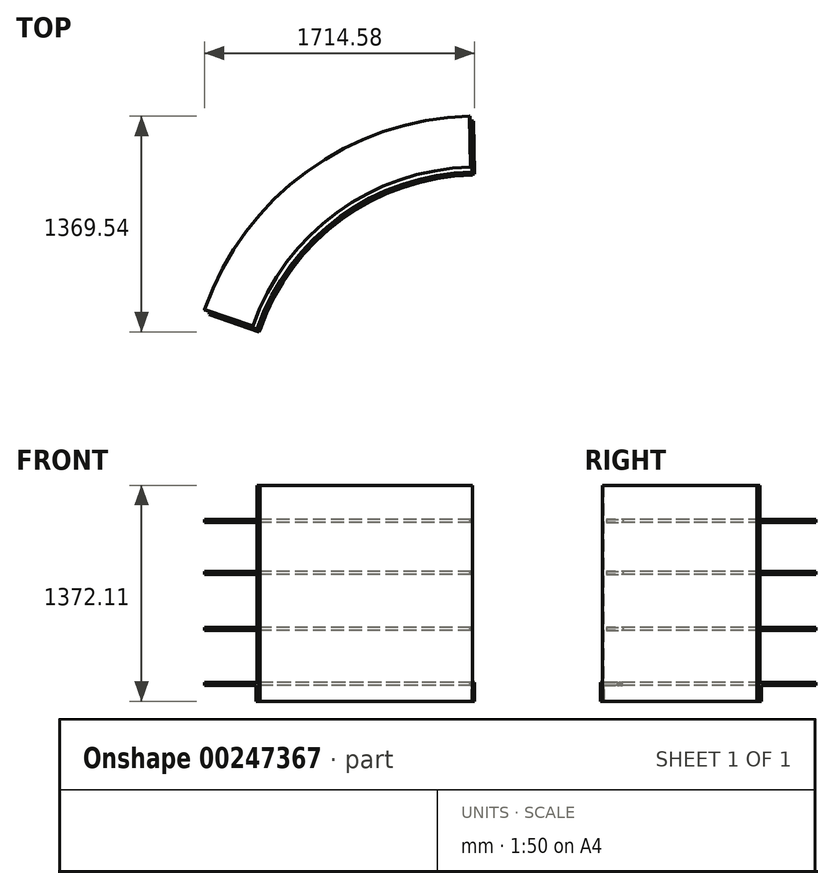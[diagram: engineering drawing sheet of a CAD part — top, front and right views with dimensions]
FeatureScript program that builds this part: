
annotation { "Feature Type Name" : "Feature", "Feature Type Description" : "" }
export const myFeature = defineFeature(function(context is Context, id is Id, definition is map)
    precondition{}
    {
        {
            var Q0;
            Q0=qCreatedBy(makeId("Top.planeOp"),FACE);
            var sketch = newSketch(context, id + "F0", { "sketchPlane" : qUnion([Q0])});
            skCircle(sketch, "E0", {"center": v(0, 0) * mm, "radius": 1828.8 * mm});
            skLineSegment(sketch, "E1", {"start": v(0, 0) * mm, "end": v(-35, 1828.47) * mm});
            skLineSegment(sketch, "E2", {"start": v(0, 0) * mm, "end": v(-1730.17, 592.48) * mm});
            skCircle(sketch, "E3", {"center": v(0, 0) * mm, "radius": 1473.2 * mm});
            skCircle(sketch, "E4", {"center": v(0, 0) * mm, "radius": 1492.76 * mm});
            skLineSegment(sketch, "E5.0", {"start": v(2.06, 6) * mm, "end": v(-1728.1, 598.5) * mm});
            skLineSegment(sketch, "E6.0", {"start": v(-6.35, -0.12) * mm, "end": v(-41.35, 1828.34) * mm});
            skLineSegment(sketch, "E7", {"start": v(-40.62, 1790.24) * mm, "end": v(-34.27, 1790.37) * mm});
            skLineSegment(sketch, "E8", {"start": v(-1692.06, 586.15) * mm, "end": v(-1694.12, 580.14) * mm});
            skCircle(sketch, "E9", {"center": v(-85.5, 1480.26) * mm, "radius": 2.5 * mm});
            skCircle(sketch, "E10.1.0", {"center": v(-270.91, 1457.77) * mm, "radius": 2.5 * mm});
            skCircle(sketch, "E10.2.0", {"center": v(-452.03, 1412.14) * mm, "radius": 2.5 * mm});
            skCircle(sketch, "E10.3.0", {"center": v(-625.97, 1344.1) * mm, "radius": 2.5 * mm});
            skCircle(sketch, "E10.4.0", {"center": v(-789.99, 1254.75) * mm, "radius": 2.5 * mm});
            skCircle(sketch, "E10.5.0", {"center": v(-941.46, 1145.48) * mm, "radius": 2.5 * mm});
            skCircle(sketch, "E10.6.0", {"center": v(-1078, 1018.03) * mm, "radius": 2.5 * mm});
            skCircle(sketch, "E10.7.0", {"center": v(-1197.43, 874.43) * mm, "radius": 2.5 * mm});
            skCircle(sketch, "E10.8.0", {"center": v(-1297.86, 716.95) * mm, "radius": 2.5 * mm});
            skCircle(sketch, "E10.9.0", {"center": v(-1377.7, 548.1) * mm, "radius": 2.5 * mm});
            skLineSegment(sketch, "E10.anchor1", {"start": v(0, 0) * mm, "end": v(-85.5, 1480.26) * mm, "construction": true});
            skLineSegment(sketch, "E10.anchor2", {"start": v(0, 0) * mm, "end": v(-1377.7, 548.1) * mm, "construction": true});
            skLineSegment(sketch, "E11.0", {"start": v(3.09, 9.01) * mm, "end": v(-1727.08, 601.5) * mm});
            skLineSegment(sketch, "E12.0", {"start": v(-9.52, -0.18) * mm, "end": v(-44.52, 1828.28) * mm});
            skCircle(sketch, "E13.0", {"center": v(0, 0) * mm, "radius": 1505.46 * mm});
            skCircle(sketch, "E14.0", {"center": v(0, 0) * mm, "radius": 1453.64 * mm});
            skLineSegment(sketch, "E15", {"start": v(2.06, 6) * mm, "end": v(-758.66, 1049.34) * mm});
            skSolve(sketch);
        }
        {
            var Q0;
            {var subQ0=sQuery(id+"F0.wireOp",EDGE,"E12.0");var subQ1=sQuery(id+"F0.wireOp",EDGE,"E0");var subQ2=makeQuery(id+"F0.imprint","INTERSECT",VERTEX,{"derivedFrom":[subQ1,subQ0]});Q0=makeQuery(id+"F0.imprint","IMPRINT",FACE,{"disambiguationData":[TD([[makeQuery(id+"F0.imprint","IMPRINT",EDGE,{"disambiguationData":[TD([[subQ2,-1.0]])],"derivedFrom":subQ1}),1.0]])]});}
            extrude(context, id + "F1", {"entities" : qUnion([Q0]), "depth" : 19.56 * mm});
        }
        {
            var Q0;
            Q0=makeQuery(id+"F1.opExtrude","SWEPT_BODY",BODY,{"disambiguationData":[OSD([sQuery(id+"F0.wireOp",EDGE,"E0"),sQuery(id+"F0.wireOp",EDGE,"E4"),sQuery(id+"F0.wireOp",EDGE,"E11.0"),sQuery(id+"F0.wireOp",EDGE,"E12.0")])]});
            transform(context, id + "F2", {"entities" : qUnion([Q0]), "transformType" : TransformType.TRANSLATION_3D, "dx" : 0 * mm, "dy" : 0 * mm, "dz" : 508 * mm, "makeCopy" : false});
        }
        {
            var Q0;
            {var subQ0=sQuery(id+"F0.wireOp",EDGE,"E12.0");var subQ1=sQuery(id+"F0.wireOp",EDGE,"E0");var subQ2=makeQuery(id+"F0.imprint","INTERSECT",VERTEX,{"derivedFrom":[subQ1,subQ0]});Q0=makeQuery(id+"F0.imprint","IMPRINT",FACE,{"disambiguationData":[TD([[makeQuery(id+"F0.imprint","IMPRINT",EDGE,{"disambiguationData":[TD([[subQ2,-1.0]])],"derivedFrom":subQ1}),1.0]])]});}
            var Q1;
            {var subQ2=sQuery(id+"F0.wireOp",EDGE,"E0");var subQ6=sQuery(id+"F0.wireOp",EDGE,"E11.0");var subQ8=makeQuery(id+"F0.imprint","INTERSECT",VERTEX,{"derivedFrom":[subQ2,subQ6]});Q1=makeQuery(id+"F0.imprint","IMPRINT",FACE,{"disambiguationData":[TD([[makeQuery(id+"F0.imprint","IMPRINT",EDGE,{"disambiguationData":[TD([[subQ8,-1.0]])],"derivedFrom":subQ2}),1.0]])]});}
            var Q2;
            {var subQ0=sQuery(id+"F0.wireOp",EDGE,"E8");Q2=makeQuery(id+"F0.imprint","IMPRINT",FACE,{"disambiguationData":[TD([[makeQuery(id+"F0.imprint","IMPRINT",EDGE,{"derivedFrom":subQ0}),1.0]])]});}
            var Q3;
            {var subQ0=sQuery(id+"F0.wireOp",EDGE,"E3");var subQ1=sQuery(id+"F0.wireOp",EDGE,"E2");var subQ2=makeQuery(id+"F0.imprint","INTERSECT",VERTEX,{"derivedFrom":[subQ1,subQ0]});Q3=makeQuery(id+"F0.imprint","IMPRINT",FACE,{"disambiguationData":[TD([[makeQuery(id+"F0.imprint","IMPRINT",EDGE,{"disambiguationData":[TD([[subQ2,-1.0]])],"derivedFrom":subQ1}),-1.0]])]});}
            var Q4;
            {var subQ0=sQuery(id+"F0.wireOp",EDGE,"E11.0");var subQ1=sQuery(id+"F0.wireOp",EDGE,"E3");var subQ2=makeQuery(id+"F0.imprint","INTERSECT",VERTEX,{"derivedFrom":[subQ1,subQ0]});Q4=makeQuery(id+"F0.imprint","IMPRINT",FACE,{"disambiguationData":[TD([[makeQuery(id+"F0.imprint","IMPRINT",EDGE,{"disambiguationData":[TD([[subQ2,-1.0]])],"derivedFrom":subQ1}),-1.0]])]});}
            var Q5;
            Q5=makeQuery(id+"F0.imprint","IMPRINT",FACE,{"disambiguationData":[TD([[makeQuery(id+"F0.imprint","IMPRINT",EDGE,{"derivedFrom":sQuery(id+"F0.wireOp",EDGE,"E9")}),-1.0]])]});
            var Q6;
            {var subQ0=sQuery(id+"F0.wireOp",EDGE,"E6.0");var subQ2=sQuery(id+"F0.wireOp",EDGE,"E0");var subQ3=makeQuery(id+"F0.imprint","INTERSECT",VERTEX,{"derivedFrom":[subQ2,subQ0]});Q6=makeQuery(id+"F0.imprint","IMPRINT",FACE,{"disambiguationData":[TD([[makeQuery(id+"F0.imprint","IMPRINT",EDGE,{"disambiguationData":[TD([[subQ3,-1.0]])],"derivedFrom":subQ2}),1.0]])]});}
            var Q7;
            {var subQ0=sQuery(id+"F0.wireOp",EDGE,"E7");Q7=makeQuery(id+"F0.imprint","IMPRINT",FACE,{"disambiguationData":[TD([[makeQuery(id+"F0.imprint","IMPRINT",EDGE,{"derivedFrom":subQ0}),-1.0]])]});}
            var Q8;
            {var subQ0=sQuery(id+"F0.wireOp",EDGE,"E3");var subQ1=sQuery(id+"F0.wireOp",EDGE,"E1");var subQ2=makeQuery(id+"F0.imprint","INTERSECT",VERTEX,{"derivedFrom":[subQ1,subQ0]});Q8=makeQuery(id+"F0.imprint","IMPRINT",FACE,{"disambiguationData":[TD([[makeQuery(id+"F0.imprint","IMPRINT",EDGE,{"disambiguationData":[TD([[subQ2,-1.0]])],"derivedFrom":subQ1}),1.0]])]});}
            var Q9;
            {var subQ0=sQuery(id+"F0.wireOp",EDGE,"E6.0");var subQ1=sQuery(id+"F0.wireOp",EDGE,"E3");var subQ2=makeQuery(id+"F0.imprint","INTERSECT",VERTEX,{"derivedFrom":[subQ1,subQ0]});Q9=makeQuery(id+"F0.imprint","IMPRINT",FACE,{"disambiguationData":[TD([[makeQuery(id+"F0.imprint","IMPRINT",EDGE,{"disambiguationData":[TD([[subQ2,-1.0]])],"derivedFrom":subQ1}),-1.0]])]});}
            var Q10;
            Q10=makeQuery(id+"F0.imprint","IMPRINT",FACE,{"disambiguationData":[TD([[makeQuery(id+"F0.imprint","IMPRINT",EDGE,{"derivedFrom":sQuery(id+"F0.wireOp",EDGE,"E10.6.0")}),1.0]])]});
            var Q11;
            Q11=makeQuery(id+"F0.imprint","IMPRINT",FACE,{"disambiguationData":[TD([[makeQuery(id+"F0.imprint","IMPRINT",EDGE,{"derivedFrom":sQuery(id+"F0.wireOp",EDGE,"E10.8.0")}),1.0]])]});
            var Q12;
            Q12=makeQuery(id+"F0.imprint","IMPRINT",FACE,{"disambiguationData":[TD([[makeQuery(id+"F0.imprint","IMPRINT",EDGE,{"derivedFrom":sQuery(id+"F0.wireOp",EDGE,"E10.7.0")}),1.0]])]});
            var Q13;
            Q13=makeQuery(id+"F0.imprint","IMPRINT",FACE,{"disambiguationData":[TD([[makeQuery(id+"F0.imprint","IMPRINT",EDGE,{"derivedFrom":sQuery(id+"F0.wireOp",EDGE,"E10.9.0")}),1.0]])]});
            var Q14;
            Q14=makeQuery(id+"F0.imprint","IMPRINT",FACE,{"disambiguationData":[TD([[makeQuery(id+"F0.imprint","IMPRINT",EDGE,{"derivedFrom":sQuery(id+"F0.wireOp",EDGE,"E10.5.0")}),1.0]])]});
            var Q15;
            Q15=makeQuery(id+"F0.imprint","IMPRINT",FACE,{"disambiguationData":[TD([[makeQuery(id+"F0.imprint","IMPRINT",EDGE,{"derivedFrom":sQuery(id+"F0.wireOp",EDGE,"E10.3.0")}),1.0]])]});
            var Q16;
            Q16=makeQuery(id+"F0.imprint","IMPRINT",FACE,{"disambiguationData":[TD([[makeQuery(id+"F0.imprint","IMPRINT",EDGE,{"derivedFrom":sQuery(id+"F0.wireOp",EDGE,"E10.1.0")}),1.0]])]});
            var Q17;
            Q17=makeQuery(id+"F0.imprint","IMPRINT",FACE,{"disambiguationData":[TD([[makeQuery(id+"F0.imprint","IMPRINT",EDGE,{"derivedFrom":sQuery(id+"F0.wireOp",EDGE,"E10.2.0")}),1.0]])]});
            var Q18;
            Q18=makeQuery(id+"F0.imprint","IMPRINT",FACE,{"disambiguationData":[TD([[makeQuery(id+"F0.imprint","IMPRINT",EDGE,{"derivedFrom":sQuery(id+"F0.wireOp",EDGE,"E10.4.0")}),1.0]])]});
            var Q19;
            Q19=makeQuery(id+"F0.imprint","IMPRINT",FACE,{"disambiguationData":[TD([[makeQuery(id+"F0.imprint","IMPRINT",EDGE,{"derivedFrom":sQuery(id+"F0.wireOp",EDGE,"E9")}),1.0]])]});
            var Q20;
            {var subQ0=sQuery(id+"F0.wireOp",EDGE,"E4");var subQ1=sQuery(id+"F0.wireOp",EDGE,"E2");var subQ2=makeQuery(id+"F0.imprint","INTERSECT",VERTEX,{"derivedFrom":[subQ1,subQ0]});Q20=makeQuery(id+"F0.imprint","IMPRINT",FACE,{"disambiguationData":[TD([[makeQuery(id+"F0.imprint","IMPRINT",EDGE,{"disambiguationData":[TD([[subQ2,-1.0]])],"derivedFrom":subQ1}),-1.0]])]});}
            var Q21;
            {var subQ0=sQuery(id+"F0.wireOp",EDGE,"E11.0");var subQ1=sQuery(id+"F0.wireOp",EDGE,"E4");var subQ2=makeQuery(id+"F0.imprint","INTERSECT",VERTEX,{"derivedFrom":[subQ1,subQ0]});Q21=makeQuery(id+"F0.imprint","IMPRINT",FACE,{"disambiguationData":[TD([[makeQuery(id+"F0.imprint","IMPRINT",EDGE,{"disambiguationData":[TD([[subQ2,-1.0]])],"derivedFrom":subQ1}),-1.0]])]});}
            var Q22;
            {var subQ0=sQuery(id+"F0.wireOp",EDGE,"E12.0");var subQ1=sQuery(id+"F0.wireOp",EDGE,"E4");var subQ2=makeQuery(id+"F0.imprint","INTERSECT",VERTEX,{"derivedFrom":[subQ1,subQ0]});Q22=makeQuery(id+"F0.imprint","IMPRINT",FACE,{"disambiguationData":[TD([[makeQuery(id+"F0.imprint","IMPRINT",EDGE,{"disambiguationData":[TD([[subQ2,-1.0]])],"derivedFrom":subQ1}),-1.0]])]});}
            var Q23;
            {var subQ0=sQuery(id+"F0.wireOp",EDGE,"E6.0");var subQ1=sQuery(id+"F0.wireOp",EDGE,"E4");var subQ2=makeQuery(id+"F0.imprint","INTERSECT",VERTEX,{"derivedFrom":[subQ1,subQ0]});Q23=makeQuery(id+"F0.imprint","IMPRINT",FACE,{"disambiguationData":[TD([[makeQuery(id+"F0.imprint","IMPRINT",EDGE,{"disambiguationData":[TD([[subQ2,-1.0]])],"derivedFrom":subQ1}),-1.0]])]});}
            var Q24;
            {var subQ0=sQuery(id+"F0.wireOp",EDGE,"E4");var subQ1=sQuery(id+"F0.wireOp",EDGE,"E1");var subQ2=makeQuery(id+"F0.imprint","INTERSECT",VERTEX,{"derivedFrom":[subQ1,subQ0]});Q24=makeQuery(id+"F0.imprint","IMPRINT",FACE,{"disambiguationData":[TD([[makeQuery(id+"F0.imprint","IMPRINT",EDGE,{"disambiguationData":[TD([[subQ2,-1.0]])],"derivedFrom":subQ1}),1.0]])]});}
            extrude(context, id + "F3", {"entities" : qUnion([Q0, Q1, Q2, Q3, Q4, Q5, Q6, Q7, Q8, Q9, Q10, Q11, Q12, Q13, Q14, Q15, Q16, Q17, Q18, Q19, Q20, Q21, Q22, Q23, Q24]), "oppositeDirection" : true, "depth" : 19.56 * mm});
        }
        {
            var Q0;
            Q0=makeQuery(id+"F1.opExtrude","SWEPT_BODY",BODY,{"disambiguationData":[OSD([sQuery(id+"F0.wireOp",EDGE,"E0"),sQuery(id+"F0.wireOp",EDGE,"E4"),sQuery(id+"F0.wireOp",EDGE,"E11.0"),sQuery(id+"F0.wireOp",EDGE,"E12.0")])]});
            transform(context, id + "F4", {"entities" : qUnion([Q0]), "transformType" : TransformType.TRANSLATION_3D, "dx" : 0 * mm, "dy" : 0 * mm, "dz" : 381 * mm, "makeCopy" : true});
        }
        {
            var Q0;
            Q0=makeQuery(id+"F4.opPattern","COPY",BODY,{"derivedFrom":makeQuery(id+"F1.opExtrude","SWEPT_BODY",BODY,{"disambiguationData":[OSD([sQuery(id+"F0.wireOp",EDGE,"E0"),sQuery(id+"F0.wireOp",EDGE,"E4"),sQuery(id+"F0.wireOp",EDGE,"E11.0"),sQuery(id+"F0.wireOp",EDGE,"E12.0")])]}),"instanceName":"1"});
            transform(context, id + "F5", {"entities" : qUnion([Q0]), "transformType" : TransformType.TRANSLATION_3D, "dx" : 0 * mm, "dy" : 0 * mm, "dz" : 381 * mm, "makeCopy" : true});
        }
        {
            var Q0;
            Q0=makeQuery(id+"F3.opExtrude","SWEPT_FACE",FACE,{"disambiguationData":[OSD([sQuery(id+"F0.wireOp",EDGE,"E2")])]});
            var sketch = newSketch(context, id + "F6", { "sketchPlane" : qUnion([Q0])});
            skLineSegment(sketch, "E16.bottom", {"start": v(-1828.79, -121.16) * mm, "end": v(-1453.63, -121.16) * mm});
            skLineSegment(sketch, "E16.top", {"start": v(-1625.59, 1250.44) * mm, "end": v(-1453.63, 1250.44) * mm});
            skLineSegment(sketch, "E16.left", {"start": v(-1828.79, -121.16) * mm, "end": v(-1828.79, 1047.24) * mm});
            skLineSegment(sketch, "E16.right", {"start": v(-1453.63, -121.16) * mm, "end": v(-1453.63, 1250.44) * mm});
            skPoint(sketch, "E17.visualSharp", {"position": v(-1828.79, 1250.44) * mm});
            skArc(sketch, "E17.filletArc", {"start": v(-1625.59, 1250.44) * mm, "mid": v(-1769.27, 1190.93) * mm, "end": v(-1828.79, 1047.24) * mm});
            skLineSegment(sketch, "E18.bottom", {"start": v(-1790.7, 0) * mm, "end": v(-1453.63, 0) * mm});
            skLineSegment(sketch, "E18.top", {"start": v(-1790.7, -19.56) * mm, "end": v(-1453.63, -19.56) * mm});
            skLineSegment(sketch, "E18.left", {"start": v(-1790.7, 0) * mm, "end": v(-1790.7, -19.56) * mm});
            skLineSegment(sketch, "E18.right", {"start": v(-1453.63, 0) * mm, "end": v(-1453.63, -19.56) * mm});
            skLineSegment(sketch, "E19.bottom", {"start": v(-1453.63, -121.16) * mm, "end": v(-1473.19, -121.16) * mm});
            skLineSegment(sketch, "E19.top", {"start": v(-1453.63, 1250.44) * mm, "end": v(-1473.19, 1250.44) * mm});
            skLineSegment(sketch, "E19.right", {"start": v(-1473.19, -121.16) * mm, "end": v(-1473.19, 1250.44) * mm});
            skSolve(sketch);
        }
        {
            var Q0;
            Q0=makeQuery(id+"F1.opExtrude","SWEPT_BODY",BODY,{"disambiguationData":[OSD([sQuery(id+"F0.wireOp",EDGE,"E0"),sQuery(id+"F0.wireOp",EDGE,"E4"),sQuery(id+"F0.wireOp",EDGE,"E11.0"),sQuery(id+"F0.wireOp",EDGE,"E12.0")])]});
            transform(context, id + "F7", {"entities" : qUnion([Q0]), "transformType" : TransformType.TRANSLATION_3D, "dx" : 0 * mm, "dy" : 0 * mm, "dz" : -127 * mm, "makeCopy" : false});
        }
        {
            var Q0;
            Q0=makeQuery(id+"F4.opPattern","COPY",BODY,{"derivedFrom":makeQuery(id+"F1.opExtrude","SWEPT_BODY",BODY,{"disambiguationData":[OSD([sQuery(id+"F0.wireOp",EDGE,"E0"),sQuery(id+"F0.wireOp",EDGE,"E4"),sQuery(id+"F0.wireOp",EDGE,"E11.0"),sQuery(id+"F0.wireOp",EDGE,"E12.0")])]}),"instanceName":"1"});
            transform(context, id + "F8", {"entities" : qUnion([Q0]), "transformType" : TransformType.TRANSLATION_3D, "dx" : 0 * mm, "dy" : 0 * mm, "dz" : -203.2 * mm, "makeCopy" : false});
        }
        {
            var Q0;
            Q0=makeQuery(id+"F1.opExtrude","SWEPT_BODY",BODY,{"disambiguationData":[OSD([sQuery(id+"F0.wireOp",EDGE,"E0"),sQuery(id+"F0.wireOp",EDGE,"E4"),sQuery(id+"F0.wireOp",EDGE,"E11.0"),sQuery(id+"F0.wireOp",EDGE,"E12.0")])]});
            transform(context, id + "F9", {"entities" : qUnion([Q0]), "transformType" : TransformType.TRANSLATION_3D, "dx" : 0 * mm, "dy" : 0 * mm, "dz" : -50.8 * mm, "makeCopy" : false});
        }
        {
            var Q0;
            Q0=makeQuery(id+"F5.opPattern","COPY",BODY,{"derivedFrom":makeQuery(id+"F4.opPattern","COPY",BODY,{"derivedFrom":makeQuery(id+"F1.opExtrude","SWEPT_BODY",BODY,{"disambiguationData":[OSD([sQuery(id+"F0.wireOp",EDGE,"E0"),sQuery(id+"F0.wireOp",EDGE,"E4"),sQuery(id+"F0.wireOp",EDGE,"E11.0"),sQuery(id+"F0.wireOp",EDGE,"E12.0")])]}),"instanceName":"1"}),"instanceName":"1"});
            transform(context, id + "F10", {"entities" : qUnion([Q0]), "transformType" : TransformType.TRANSLATION_3D, "dx" : 0 * mm, "dy" : 0 * mm, "dz" : -254 * mm, "makeCopy" : false});
        }
        {
            var Q0;
            {var subQ0=sQuery(id+"F0.wireOp",EDGE,"E2");Q0=makeQuery(id+"F6.imprint","IMPRINT",FACE,{"disambiguationData":[TD([[makeQuery(id+"F6.imprint","IMPRINT",EDGE,{"derivedFrom":makeQuery(id+"F3.opExtrude","CAP_EDGE",EDGE,{"disambiguationData":[OSD([subQ0])],"isStart":true})}),1.0]])]});}
            var Q1;
            {var subQ5=sQuery(id+"F6.wireOp",EDGE,"E19.top");Q1=makeQuery(id+"F6.imprint","IMPRINT",FACE,{"disambiguationData":[TD([[makeQuery(id+"F6.imprint","IMPRINT",EDGE,{"derivedFrom":subQ5}),1.0]])]});}
            var Q2;
            {var subQ5=sQuery(id+"F6.wireOp",EDGE,"E19.bottom");Q2=makeQuery(id+"F6.imprint","IMPRINT",FACE,{"disambiguationData":[TD([[makeQuery(id+"F6.imprint","IMPRINT",EDGE,{"derivedFrom":subQ5}),-1.0]])]});}
            var Q3;
            {var subQ0=sQuery(id+"F6.wireOp",EDGE,"E16.right");var subQ1=sQuery(id+"F6.wireOp",EDGE,"E18.bottom");var subQ2=makeQuery(id+"F6.imprint","INTERSECT",VERTEX,{"derivedFrom":[subQ1,subQ0]});Q3=makeQuery(id+"F6.imprint","IMPRINT",FACE,{"disambiguationData":[TD([[makeQuery(id+"F6.imprint","IMPRINT",EDGE,{"disambiguationData":[TD([[subQ2,1.0]])],"derivedFrom":subQ1}),-1.0]])]});}
            var Q4;
            {var subQ6=sQuery(id+"F6.wireOp",EDGE,"E16.bottom");Q4=makeQuery(id+"F6.imprint","IMPRINT",FACE,{"disambiguationData":[TD([[makeQuery(id+"F6.imprint","IMPRINT",EDGE,{"derivedFrom":subQ6}),1.0]])]});}
            var Q5;
            {var subQ0=sQuery(id+"F6.wireOp",EDGE,"E18.left");Q5=makeQuery(id+"F6.imprint","IMPRINT",FACE,{"disambiguationData":[TD([[makeQuery(id+"F6.imprint","IMPRINT",EDGE,{"derivedFrom":subQ0}),-1.0]])]});}
            extrude(context, id + "F11", {"entities" : qUnion([Q0, Q1, Q2, Q3, Q4, Q5]), "depth" : 19.56 * mm});
        }
        {
            var Q0;
            {var subQ0=sQuery(id+"F6.wireOp",EDGE,"E18.left");Q0=makeQuery(id+"F6.imprint","IMPRINT",FACE,{"disambiguationData":[TD([[makeQuery(id+"F6.imprint","IMPRINT",EDGE,{"derivedFrom":subQ0}),-1.0]])]});}
            extrude(context, id + "F12", {"entities" : qUnion([Q0]), "operationType" : NewBodyOperationType.REMOVE, "depth" : 6.35 * mm});
        }
        {
            var Q0;
            {var subQ5=sQuery(id+"F6.wireOp",EDGE,"E19.top");Q0=makeQuery(id+"F6.imprint","IMPRINT",FACE,{"disambiguationData":[TD([[makeQuery(id+"F6.imprint","IMPRINT",EDGE,{"derivedFrom":subQ5}),1.0]])]});}
            var Q1;
            {var subQ0=sQuery(id+"F6.wireOp",EDGE,"E16.right");var subQ1=sQuery(id+"F6.wireOp",EDGE,"E18.bottom");var subQ2=makeQuery(id+"F6.imprint","INTERSECT",VERTEX,{"derivedFrom":[subQ1,subQ0]});Q1=makeQuery(id+"F6.imprint","IMPRINT",FACE,{"disambiguationData":[TD([[makeQuery(id+"F6.imprint","IMPRINT",EDGE,{"disambiguationData":[TD([[subQ2,1.0]])],"derivedFrom":subQ1}),-1.0]])]});}
            var Q2;
            {var subQ5=sQuery(id+"F6.wireOp",EDGE,"E19.bottom");Q2=makeQuery(id+"F6.imprint","IMPRINT",FACE,{"disambiguationData":[TD([[makeQuery(id+"F6.imprint","IMPRINT",EDGE,{"derivedFrom":subQ5}),-1.0]])]});}
            extrude(context, id + "F13", {"entities" : qUnion([Q0, Q1, Q2]), "operationType" : NewBodyOperationType.REMOVE, "depth" : 15.88 * mm});
        }
        {
            var Q0;
            Q0=makeQuery(id+"F11.opExtrude","SWEPT_BODY",BODY,{"disambiguationData":[OSD([sQuery(id+"F0.wireOp",EDGE,"E2"),sQuery(id+"F0.wireOp",EDGE,"E3"),sQuery(id+"F6.wireOp",EDGE,"E16.bottom"),sQuery(id+"F6.wireOp",EDGE,"E16.top"),sQuery(id+"F6.wireOp",EDGE,"E16.left"),sQuery(id+"F6.wireOp",EDGE,"E17.filletArc"),sQuery(id+"F6.wireOp",EDGE,"E18.bottom"),sQuery(id+"F6.wireOp",EDGE,"E18.top"),sQuery(id+"F6.wireOp",EDGE,"E19.bottom"),sQuery(id+"F6.wireOp",EDGE,"E19.top"),sQuery(id+"F6.wireOp",EDGE,"E16.right"),sQuery(id+"F6.wireOp",EDGE,"E19.right")])]});
            transform(context, id + "F14", {"entities" : qUnion([Q0]), "transformType" : TransformType.TRANSLATION_3D, "dx" : 0 * mm, "dy" : 6.35 * mm, "dz" : 0 * mm, "makeCopy" : false});
        }
        {
            var Q0;
            {var subQ0=sQuery(id+"F0.wireOp",EDGE,"E14.0");var subQ1=sQuery(id+"F0.wireOp",EDGE,"E2");var subQ2=makeQuery(id+"F0.imprint","INTERSECT",VERTEX,{"derivedFrom":[subQ1,subQ0]});Q0=makeQuery(id+"F0.imprint","IMPRINT",FACE,{"disambiguationData":[TD([[makeQuery(id+"F0.imprint","IMPRINT",EDGE,{"disambiguationData":[TD([[subQ2,-1.0]])],"derivedFrom":subQ1}),-1.0]])]});}
            var Q1;
            {var subQ0=sQuery(id+"F0.wireOp",EDGE,"E11.0");var subQ1=sQuery(id+"F0.wireOp",EDGE,"E3");var subQ2=makeQuery(id+"F0.imprint","INTERSECT",VERTEX,{"derivedFrom":[subQ1,subQ0]});Q1=makeQuery(id+"F0.imprint","IMPRINT",FACE,{"disambiguationData":[TD([[makeQuery(id+"F0.imprint","IMPRINT",EDGE,{"disambiguationData":[TD([[subQ2,-1.0]])],"derivedFrom":subQ1}),1.0]])]});}
            var Q2;
            {var subQ0=sQuery(id+"F0.wireOp",EDGE,"E12.0");var subQ1=sQuery(id+"F0.wireOp",EDGE,"E3");var subQ2=makeQuery(id+"F0.imprint","INTERSECT",VERTEX,{"derivedFrom":[subQ1,subQ0]});Q2=makeQuery(id+"F0.imprint","IMPRINT",FACE,{"disambiguationData":[TD([[makeQuery(id+"F0.imprint","IMPRINT",EDGE,{"disambiguationData":[TD([[subQ2,-1.0]])],"derivedFrom":subQ1}),1.0]])]});}
            var Q3;
            {var subQ0=sQuery(id+"F0.wireOp",EDGE,"E6.0");var subQ1=sQuery(id+"F0.wireOp",EDGE,"E3");var subQ2=makeQuery(id+"F0.imprint","INTERSECT",VERTEX,{"derivedFrom":[subQ1,subQ0]});Q3=makeQuery(id+"F0.imprint","IMPRINT",FACE,{"disambiguationData":[TD([[makeQuery(id+"F0.imprint","IMPRINT",EDGE,{"disambiguationData":[TD([[subQ2,-1.0]])],"derivedFrom":subQ1}),1.0]])]});}
            var Q4;
            {var subQ0=sQuery(id+"F0.wireOp",EDGE,"E14.0");var subQ1=sQuery(id+"F0.wireOp",EDGE,"E1");var subQ2=makeQuery(id+"F0.imprint","INTERSECT",VERTEX,{"derivedFrom":[subQ1,subQ0]});Q4=makeQuery(id+"F0.imprint","IMPRINT",FACE,{"disambiguationData":[TD([[makeQuery(id+"F0.imprint","IMPRINT",EDGE,{"disambiguationData":[TD([[subQ2,-1.0]])],"derivedFrom":subQ1}),1.0]])]});}
            extrude(context, id + "F15", {"entities" : qUnion([Q0, Q1, Q2, Q3, Q4]), "depth" : 1371.6 * mm});
        }
        {
            var Q0;
            Q0=makeQuery(id+"F15.opExtrude","SWEPT_BODY",BODY,{"disambiguationData":[OSD([sQuery(id+"F0.wireOp",EDGE,"E1"),sQuery(id+"F0.wireOp",EDGE,"E2"),sQuery(id+"F0.wireOp",EDGE,"E3"),sQuery(id+"F0.wireOp",EDGE,"E14.0")])]});
            transform(context, id + "F16", {"entities" : qUnion([Q0]), "transformType" : TransformType.TRANSLATION_3D, "dx" : 0 * mm, "dy" : 0 * mm, "dz" : -101.6 * mm, "makeCopy" : false});
        }
        {
            var Q0;
            Q0=makeQuery(id+"F15.opExtrude","SWEPT_BODY",BODY,{"disambiguationData":[OSD([sQuery(id+"F0.wireOp",EDGE,"E1"),sQuery(id+"F0.wireOp",EDGE,"E2"),sQuery(id+"F0.wireOp",EDGE,"E3"),sQuery(id+"F0.wireOp",EDGE,"E14.0")])]});
            transform(context, id + "F17", {"entities" : qUnion([Q0]), "transformType" : TransformType.TRANSLATION_3D, "dx" : 0 * mm, "dy" : 0 * mm, "dz" : -19.05 * mm, "makeCopy" : false});
        }
        {
            var Q0;
            Q0=sQuery(id+"F0.wireOp",EDGE,"E15");
            extrude(context, id + "F18", {"bodyType" : ToolBodyType.SURFACE, "surfaceEntities" : qUnion([Q0]), "depth" : 254 * mm});
        }
        {
            var Q0;
            Q0=makeQuery(id+"F11.opExtrude","SWEPT_BODY",BODY,{"disambiguationData":[OSD([sQuery(id+"F0.wireOp",EDGE,"E2"),sQuery(id+"F0.wireOp",EDGE,"E3"),sQuery(id+"F6.wireOp",EDGE,"E16.bottom"),sQuery(id+"F6.wireOp",EDGE,"E16.top"),sQuery(id+"F6.wireOp",EDGE,"E16.left"),sQuery(id+"F6.wireOp",EDGE,"E17.filletArc"),sQuery(id+"F6.wireOp",EDGE,"E18.bottom"),sQuery(id+"F6.wireOp",EDGE,"E18.top"),sQuery(id+"F6.wireOp",EDGE,"E19.bottom"),sQuery(id+"F6.wireOp",EDGE,"E19.top"),sQuery(id+"F6.wireOp",EDGE,"E16.right"),sQuery(id+"F6.wireOp",EDGE,"E19.right")])]});
            var Q1;
            Q1=makeQuery(id+"F18.opExtrude","SWEPT_FACE",FACE,{"disambiguationData":[OSD([sQuery(id+"F0.wireOp",EDGE,"E15")])]});
            mirror(context, id + "F19", {"entities" : qUnion([Q0]), "mirrorPlane" : qUnion([Q1])});
        }
        {
            var Q0;
            Q0=makeQuery(id+"F18.opExtrude","SWEPT_BODY",BODY,{"disambiguationData":[OSD([sQuery(id+"F0.wireOp",EDGE,"E15")])]});
            deleteBodies(context, id + "F20", {"entities" : qUnion([Q0])});
        }
        {
            var Q0;
            Q0=makeQuery(id+"F19.opPattern","COPY",BODY,{"derivedFrom":makeQuery(id+"F11.opExtrude","SWEPT_BODY",BODY,{"disambiguationData":[OSD([sQuery(id+"F0.wireOp",EDGE,"E2"),sQuery(id+"F0.wireOp",EDGE,"E3"),sQuery(id+"F6.wireOp",EDGE,"E16.bottom"),sQuery(id+"F6.wireOp",EDGE,"E16.top"),sQuery(id+"F6.wireOp",EDGE,"E16.left"),sQuery(id+"F6.wireOp",EDGE,"E17.filletArc"),sQuery(id+"F6.wireOp",EDGE,"E18.bottom"),sQuery(id+"F6.wireOp",EDGE,"E18.top"),sQuery(id+"F6.wireOp",EDGE,"E19.bottom"),sQuery(id+"F6.wireOp",EDGE,"E19.top"),sQuery(id+"F6.wireOp",EDGE,"E16.right"),sQuery(id+"F6.wireOp",EDGE,"E19.right")])]}),"instanceName":"1"});
            transform(context, id + "F21", {"entities" : qUnion([Q0]), "transformType" : TransformType.TRANSLATION_3D, "dx" : -7.62 * mm, "dy" : 0 * mm, "dz" : 0 * mm, "makeCopy" : false});
        }
    });
